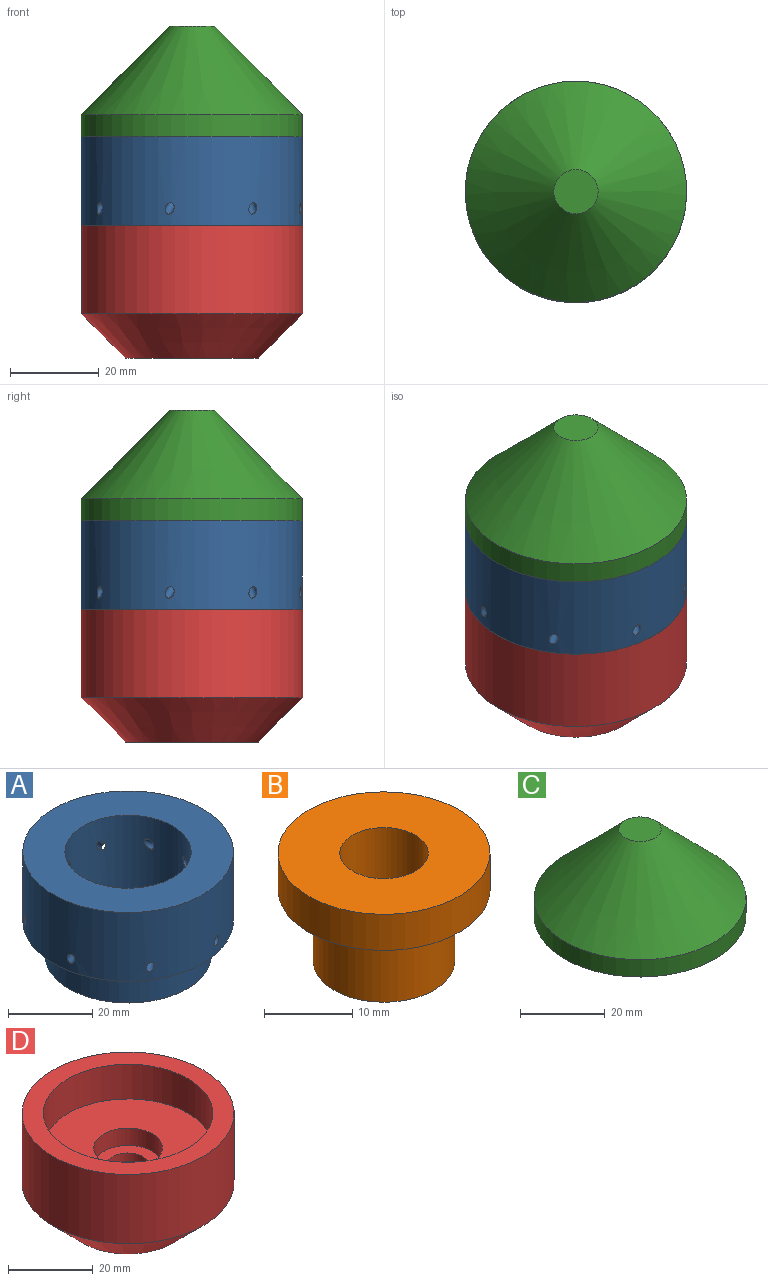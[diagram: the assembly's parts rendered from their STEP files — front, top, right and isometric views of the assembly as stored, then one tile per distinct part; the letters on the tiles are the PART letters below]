
ASSEMBLY  parts=4 mates=3
PART A: 16 faces, bbox 51.5x51.5x30 mm
  f0: cylinder r=8.25mm len=16.5mm, axis (0,0,1), area 248.8mm2, adj f1,f7
  f1: plane 39.5x39.5mm, normal (0,0,-1), area 1011.6mm2, adj f0,f2
  f2: cylinder r=19.75mm len=39.5mm, axis (0,0,1), area 1240.9mm2, adj f1,f3
  f3: plane 50x50mm, normal (0,0,-1), area 738.1mm2, adj f2,f4
  f4: cylinder r=25mm len=50mm, axis (0,0,1), area 3108.3mm2, adj f3,f5,f8,f9,f10,f11,f12,f13
  f5: plane 50x50mm, normal (0,0,1), area 1256.6mm2, adj f4,f6
  f6: cylinder r=15mm len=30mm, axis (0,0,1), area 2337.8mm2, adj f5,f7,f8,f9,f10,f11,f12,f13
  f7: plane 30x30mm, normal (0,0,1), area 493mm2, adj f0,f6
  f8: cylinder r=1mm len=11.27mm, axis (-0.61,-0.5,-0.61), area 86.9mm2, adj f4,f6
  f9: cylinder r=1mm len=13.67mm, axis (-0.79,0.08,-0.61), area 86.9mm2, adj f4,f6
  f10: cylinder r=1mm len=11.27mm, axis (-0.5,0.61,-0.61), area 86.9mm2, adj f4,f6
  f11: cylinder r=1mm len=13.67mm, axis (0.08,0.79,-0.61), area 86.9mm2, adj f4,f6
  f12: cylinder r=1mm len=11.27mm, axis (0.61,0.5,-0.61), area 86.9mm2, adj f4,f6
  f13: cylinder r=1mm len=13.67mm, axis (0.79,-0.08,-0.61), area 86.9mm2, adj f4,f6
  f14: cylinder r=1mm len=11.27mm, axis (0.5,-0.61,-0.61), area 86.9mm2, adj f4,f6
  f15: cylinder r=1mm len=13.67mm, axis (-0.08,-0.79,-0.61), area 86.9mm2, adj f4,f6
PART B: 6 faces, bbox 24x24x15 mm
  f0: plane 16x16mm, normal (0,0,-1), area 122.5mm2, adj f1,f5
  f1: cylinder r=8mm len=16mm, axis (0,0,-1), area 502.7mm2, adj f0,f2
  f2: plane 24x24mm, normal (0,0,-1), area 251.3mm2, adj f1,f3
  f3: cylinder r=12mm len=24mm, axis (0,0,-1), area 377mm2, adj f2,f4
  f4: plane 24x24mm, normal (0,0,1), area 373.8mm2, adj f3,f5
  f5: cylinder r=5mm len=15mm, axis (0,0,1), area 471.2mm2, adj f0,f4
PART C: 7 faces, bbox 50x50x30 mm
  f0: plane 50x50mm, normal (0,0,-1), area 1256.6mm2, adj f1,f6
  f1: cylinder r=25mm len=50mm, axis (0,0,1), area 785.4mm2, adj f0,f2
  f2: cone r=25mm half-angle=45deg, axis (0,0,-1), area 2665.7mm2, adj f1,f3
  f3: plane 10x10mm, normal (0,0,1), area 78.5mm2, adj f2
  f4: cone r=12mm half-angle=45deg, axis (0,0,-1), area 639.8mm2, adj f5
  f5: plane 30x30mm, normal (0,0,-1), area 254.5mm2, adj f4,f6
  f6: cylinder r=15mm len=30mm, axis (0,0,1), area 471.2mm2, adj f0,f5
PART D: 11 faces, bbox 50x50x30 mm
  f0: cylinder r=25mm len=50mm, axis (0,0,-1), area 3141.6mm2, adj f1,f5
  f1: plane 50x50mm, normal (0,0,1), area 706.9mm2, adj f0,f3
  f2: plane 30x30mm, normal (0,0,-1), area 235.4mm2, adj f5,f9
  f3: cylinder r=20mm len=40mm, axis (0,0,1), area 1256.6mm2, adj f1,f4
  f4: plane 40x40mm, normal (0,0,1), area 1050.5mm2, adj f3,f6
  f5: cone r=25mm half-angle=45deg, axis (0,0,1), area 1777.2mm2, adj f0,f2
  f6: cylinder r=8.1mm len=16.2mm, axis (0,0,1), area 254.5mm2, adj f4,f7
  f7: plane 16.2x16.2mm, normal (0,0,1), area 127.6mm2, adj f6,f8
  f8: cylinder r=5mm len=10mm, axis (0,0,-1), area 78.5mm2, adj f7,f10
  f9: cylinder r=12.25mm len=24.5mm, axis (0,0,-1), area 962.1mm2, adj f2,f10
  f10: plane 24.5x24.5mm, normal (0,0,-1), area 392.9mm2, adj f8,f9
PLACE A rot(axis=(0,0,1),111deg) t=(12.16,17.5,0.52)mm
PLACE B t=(12.16,17.5,5.72)mm
PLACE C rot(axis=(0,0,1),111deg) t=(12.16,17.5,0.52)mm
PLACE D t=(12.16,17.5,0.72)mm fixed
MATE revolute A.f0 <-> D.f3  axis (0,0,-1) through (12.16,17.5,20.72)mm
MATE fastened B.f1 <-> D.f6  axis (0,0,1) through (12.16,17.5,20.72)mm
MATE fastened C.f1 <-> A.f0  axis (0,0,-1) through (12.16,17.5,50.72)mm
